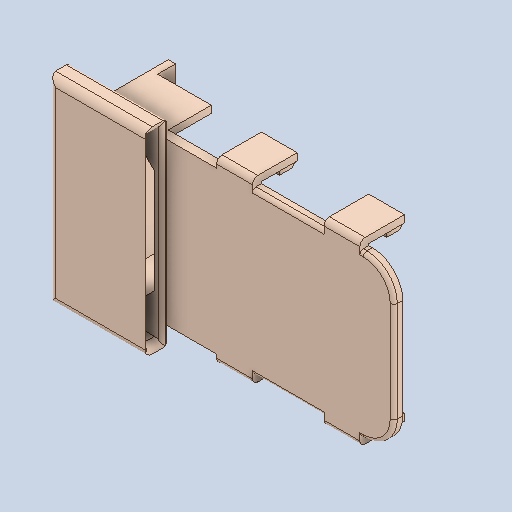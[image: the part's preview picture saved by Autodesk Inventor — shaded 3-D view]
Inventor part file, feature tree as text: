
AUTODESK INVENTOR PART (.ipt)
format: ipt  version: 2023.3 (Build 273359000, 359)  size: 419,328 bytes
history: native  units: in
note: dims shown in document units (in); Inventor stores cm internally (conversion verified against a paired STEP export)
features: reference x26, extrude x9, sketch x8, fillet x7, other x6, chamfer x2, plane x1
ambient origin geometry x8: Origin, YZ Plane, XZ Plane, XY Plane, X Axis, Y Axis, Z Axis, Center Point
bodies: Solid1 (feature_tree)
feature tree (59):
  plane  "Work Plane1"
  extrude  "main"  Depth=0.0787in TaperAngle=0.0deg
  extrude  "flaps"  Depth=0.0157in TaperAngle=0.0deg
  sketch  "Sketch9"  dims[d50=0.0157in d67=0.0472in d68=0.0157in d69=0.0in d70=0.0in]
  extrude  "Extrusion13"  Depth=0.0079in
  extrude  "Extrusion18"  Depth=0.0039in
  extrude  "Extrusion19"  Depth=0.0039in
  extrude  "Extrusion20"  Depth=0.0157in TaperAngle=0.0deg
  fillet  "Fillet4"  Radius=0.0157in
  fillet  "Fillet5"  Radius=0.2126in
  fillet  "Fillet6"  Radius=0.4331in
  extrude  "Extrusion21"  Depth=0.0157in
  fillet  "Fillet7"  Radius=0.0256in
  fillet  "Fillet9"  Radius=0.0157in
  fillet  "Fillet10"  Radius=0.0157in
  extrude  "Extrusion22"  Depth=0.0157in
  extrude  "Extrusion23"  Depth=0.0157in
  chamfer  "Chamfer6"  Distance=0.0079in
  chamfer  "Chamfer7"  Distance=0.1969in
  fillet  "Fillet11"  Radius=0.0118in
  sketch  "Sketch1"  dims[d2=0.0197in d3=0.0in d6=0.0787in d7=0.0in]
  reference  "Reference10"
  reference  "Reference11"
  reference  "Reference31"
  reference  "Reference32"
  reference  "Reference33"
  reference  "Reference34"
  reference  "Reference35"
  reference  "Reference36"
  reference  "Reference37"
  reference  "Reference38"
  reference  "Reference39"
  reference  "Reference40"
  reference  "Reference41"
  reference  "Reference42"
  sketch  "Sketch18"  dims[d89=0.0197in d90=0.0079in]
  reference  "Reference43"
  reference  "Reference44"
  reference  "Reference45"
  sketch  "Sketch19"  dims[d91=0.0039in d92=0.0039in]
  reference  "Reference48"
  sketch  "Sketch20"  dims[d93=0.0039in d94=0.0039in]
  sketch  "Sketch21"  dims[d95=0.0079in d96=0.0945in d97=0.0in d98=0.0157in d99=0.0in d100=0.2126in d101=0.4331in]
  sketch  "Sketch22"  dims[d102=0.0787in d105=0.0108in d106=0.0256in d107=0.0157in d108=0.0157in]
  reference  "Reference49"
  reference  "Reference50"
  reference  "Reference51"
  reference  "Reference52"
  reference  "Reference53"
  reference  "Reference54"
  reference  "Reference55"
  reference  "Reference56"
  sketch  "Sketch23"  dims[d109=0.1969in d110=0.0in d111=0.0157in d112=0.0157in d113=0.0079in d118=0.1969in d119=0.0in d120=0.0118in d121=0.0in d122=0.0in d123=0.0in d125=0.0079in d126=0.0669in d127=0.0276in d134=0.0039in d135=0.0079in d136=0.0039in d137=0.0039in d138=0.0039in d139=0.0039in d140=0.0039in d141=0.0118in d142=0.0in d143=0.0118in d144=0.0in d145=0.0079in d146=0.0591in d147=45.0deg d148=0.0472in d149=0.0787in d150=45.0deg d151=0.0079in d38=0.0in d39=0.0in d40=0.0in d41=0.0in d61=0.0in d62=0.0in d63=0.0in d64=0.0in d83=0.0197in d84=0.0344in d85=0.0197in d86=0.0344in]
  parser-record x2  (decoder bookkeeping rows leaked as tree rows — omitted from the tree; the rows remain in map.json)
  other  "np2alpha_full_assembly.iam"
  other  "np2alpha_main_chassis:1"
  other  "np2a_assembly.iam"
  other  "np2a:1"
note: 2 file-system paths scrubbed to <path> (originals preserved in map.json)
